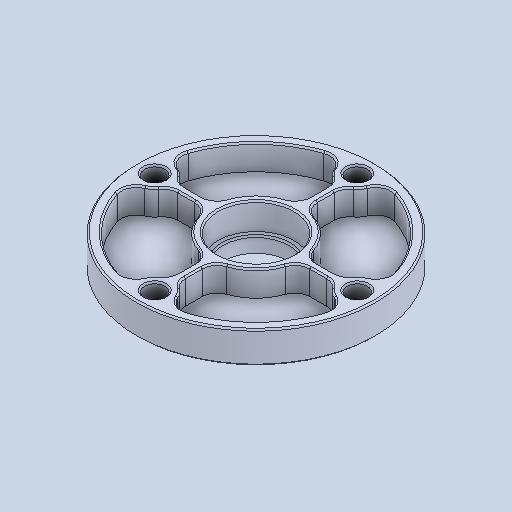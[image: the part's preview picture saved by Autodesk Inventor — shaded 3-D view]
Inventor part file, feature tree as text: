
AUTODESK INVENTOR PART (.ipt)
format: ipt  version: 2024.2 (Build 282272000, 272)  size: 276,992 bytes
history: native  units: in
note: dims shown in document units (in); Inventor stores cm internally (conversion verified against a paired STEP export)
features: chamfer x1
ambient origin geometry x8: Origin, YZ Plane, XZ Plane, XY Plane, X Axis, Y Axis, Z Axis, Center Point
bodies: Solid1 (feature_tree)
feature tree (1):
  chamfer  "Chamfer1"  [1 undecoded]
note: 1 required parameter value undecoded (feature->parameter linkage not recoverable at this tier; creation-order binding heuristic only, values carry confidence <= 0.55)
